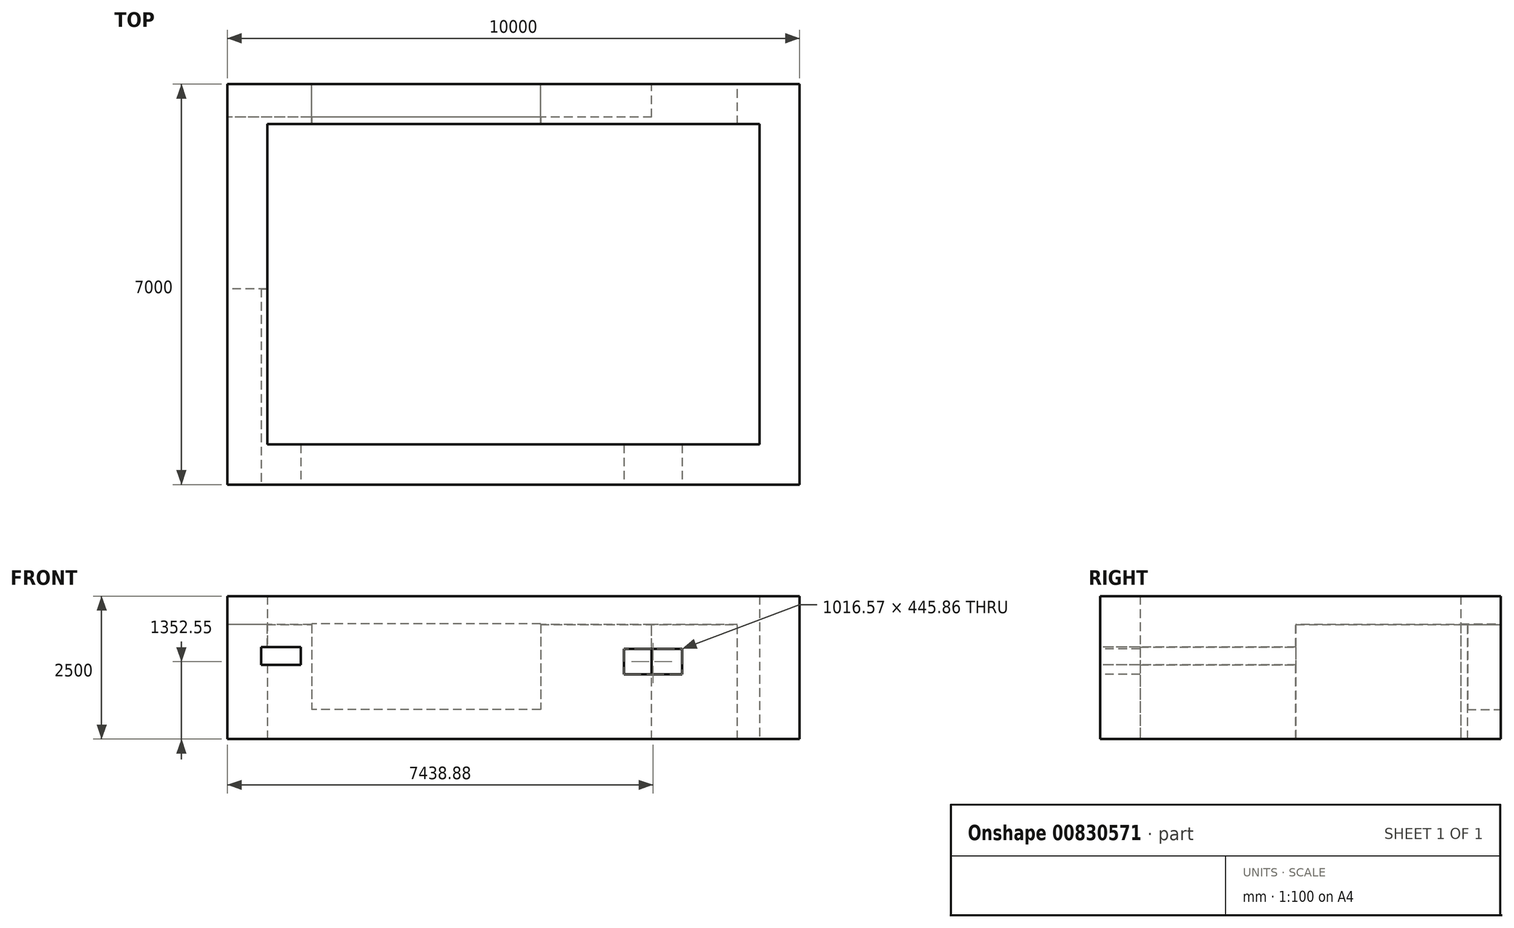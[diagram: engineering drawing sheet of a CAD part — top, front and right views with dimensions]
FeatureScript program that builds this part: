
annotation { "Feature Type Name" : "Feature", "Feature Type Description" : "" }
export const myFeature = defineFeature(function(context is Context, id is Id, definition is map)
    precondition{}
    {
        {
            var Q0;
            Q0=qCreatedBy(makeId("Top.planeOp"),FACE);
            var sketch = newSketch(context, id + "F0", { "sketchPlane" : qUnion([Q0])});
            skLineSegment(sketch, "E0.bottom", {"start": v(0, 0) * mm, "end": v(10000, 0) * mm});
            skLineSegment(sketch, "E0.top", {"start": v(0, 7000) * mm, "end": v(10000, 7000) * mm});
            skLineSegment(sketch, "E0.left", {"start": v(0, 0) * mm, "end": v(0, 7000) * mm});
            skLineSegment(sketch, "E0.right", {"start": v(10000, 0) * mm, "end": v(10000, 7000) * mm});
            skLineSegment(sketch, "E1.0", {"start": v(700, 700) * mm, "end": v(700, 6300) * mm});
            skLineSegment(sketch, "E1.1", {"start": v(700, 700) * mm, "end": v(9300, 700) * mm});
            skLineSegment(sketch, "E1.2", {"start": v(9300, 700) * mm, "end": v(9300, 6300) * mm});
            skLineSegment(sketch, "E1.3", {"start": v(700, 6300) * mm, "end": v(9300, 6300) * mm});
            skLineSegment(sketch, "E2.bottom", {"start": v(9294.84, 7000) * mm, "end": v(9300, 7000) * mm});
            skLineSegment(sketch, "E2.top", {"start": v(9294.84, 6300) * mm, "end": v(9300, 6300) * mm});
            skLineSegment(sketch, "E2.left", {"start": v(9294.84, 7000) * mm, "end": v(9294.84, 6300) * mm});
            skLineSegment(sketch, "E2.right", {"start": v(9300, 7000) * mm, "end": v(9300, 6300) * mm});
            skSolve(sketch);
        }
        {
            var Q0;
            Q0 = qSketchRegion(id + "F0", true);
            extrude(context, id + "F1", {"entities" : qUnion([Q0]), "depth" : 2500 * mm, "offsetDistance" : 25 * mm});
        }
        {
            var Q0;
            Q0=makeQuery(id+"F1.opExtrude","SWEPT_FACE",FACE,{"disambiguationData":[OSD([sQuery(id+"F0.wireOp",EDGE,"E0.top"),sQuery(id+"F0.wireOp",EDGE,"E2.bottom")])]});
            var sketch = newSketch(context, id + "F2", { "sketchPlane" : qUnion([Q0])});
            skLineSegment(sketch, "E3.bottom", {"start": v(-8914.27, 0) * mm, "end": v(-7414.27, 0) * mm});
            skLineSegment(sketch, "E3.top", {"start": v(-8914.27, 2000) * mm, "end": v(-7414.27, 2000) * mm});
            skLineSegment(sketch, "E3.left", {"start": v(-8914.27, 0) * mm, "end": v(-8914.27, 2000) * mm});
            skLineSegment(sketch, "E3.right", {"start": v(-7414.27, 0) * mm, "end": v(-7414.27, 2000) * mm});
            skLineSegment(sketch, "E4.bottom", {"start": v(-5473.14, 2015.1) * mm, "end": v(-1473.14, 2015.1) * mm});
            skLineSegment(sketch, "E4.top", {"start": v(-5473.14, 515.1) * mm, "end": v(-1473.14, 515.1) * mm});
            skLineSegment(sketch, "E4.left", {"start": v(-5473.14, 2015.1) * mm, "end": v(-5473.14, 515.1) * mm});
            skLineSegment(sketch, "E4.right", {"start": v(-1473.14, 2015.1) * mm, "end": v(-1473.14, 515.1) * mm});
            skSolve(sketch);
        }
        {
            var Q0;
            Q0=makeQuery(id+"F2.imprint","IMPRINT",FACE,{"disambiguationData":[TD([[makeQuery(id+"F2.imprint","IMPRINT",EDGE,{"derivedFrom":sQuery(id+"F2.wireOp",EDGE,"E3.bottom")}),-1.0]])]});
            var Q1;
            Q1=makeQuery(id+"F2.imprint","IMPRINT",FACE,{"disambiguationData":[TD([[makeQuery(id+"F2.imprint","IMPRINT",EDGE,{"derivedFrom":sQuery(id+"F2.wireOp",EDGE,"E4.bottom")}),-1.0]])]});
            extrude(context, id + "F3", {"entities" : qUnion([Q0, Q1]), "operationType" : NewBodyOperationType.REMOVE, "endBound" : BoundingType.UP_TO_NEXT, "oppositeDirection" : true, "depth" : 25 * mm, "offsetDistance" : 25 * mm});
        }
        {
            var Q0;
            Q0=makeQuery(id+"F1.opExtrude","SWEPT_FACE",FACE,{"disambiguationData":[OSD([sQuery(id+"F0.wireOp",EDGE,"E0.left")])]});
            var sketch = newSketch(context, id + "F4", { "sketchPlane" : qUnion([Q0])});
            skLineSegment(sketch, "E5.bottom", {"start": v(-6420.84, 2000) * mm, "end": v(-3420.84, 2000) * mm});
            skLineSegment(sketch, "E5.top", {"start": v(-6420.84, 0) * mm, "end": v(-3420.84, 0) * mm});
            skLineSegment(sketch, "E5.left", {"start": v(-6420.84, 2000) * mm, "end": v(-6420.84, 0) * mm});
            skLineSegment(sketch, "E5.right", {"start": v(-3420.84, 2000) * mm, "end": v(-3420.84, 0) * mm});
            skSolve(sketch);
        }
        {
            var Q0;
            Q0=makeQuery(id+"F4.imprint","IMPRINT",FACE,{"disambiguationData":[TD([[makeQuery(id+"F4.imprint","IMPRINT",EDGE,{"derivedFrom":sQuery(id+"F4.wireOp",EDGE,"E5.bottom")}),-1.0]])]});
            extrude(context, id + "F5", {"entities" : qUnion([Q0]), "operationType" : NewBodyOperationType.REMOVE, "endBound" : BoundingType.UP_TO_NEXT, "oppositeDirection" : true, "depth" : 25 * mm, "offsetDistance" : 25 * mm});
        }
        {
            var Q0;
            Q0=makeQuery(id+"F1.opExtrude","SWEPT_FACE",FACE,{"disambiguationData":[OSD([sQuery(id+"F0.wireOp",EDGE,"E0.bottom")])]});
            var sketch = newSketch(context, id + "F6", { "sketchPlane" : qUnion([Q0])});
            skLineSegment(sketch, "E6.bottom", {"start": v(590.4, 1611.15) * mm, "end": v(1285.95, 1611.15) * mm});
            skLineSegment(sketch, "E6.top", {"start": v(590.4, 1299.05) * mm, "end": v(1285.95, 1299.05) * mm});
            skLineSegment(sketch, "E6.left", {"start": v(590.4, 1611.15) * mm, "end": v(590.4, 1299.05) * mm});
            skLineSegment(sketch, "E6.right", {"start": v(1285.95, 1611.15) * mm, "end": v(1285.95, 1299.05) * mm});
            skLineSegment(sketch, "E7.bottom", {"start": v(6930.6, 1575.48) * mm, "end": v(7947.16, 1575.48) * mm});
            skLineSegment(sketch, "E7.top", {"start": v(6930.6, 1129.62) * mm, "end": v(7947.16, 1129.62) * mm});
            skLineSegment(sketch, "E7.left", {"start": v(6930.6, 1575.48) * mm, "end": v(6930.6, 1129.62) * mm});
            skLineSegment(sketch, "E7.right", {"start": v(7947.16, 1575.48) * mm, "end": v(7947.16, 1129.62) * mm});
            skSolve(sketch);
        }
        {
            var Q0;
            Q0=makeQuery(id+"F6.imprint","IMPRINT",FACE,{"disambiguationData":[TD([[makeQuery(id+"F6.imprint","IMPRINT",EDGE,{"derivedFrom":sQuery(id+"F6.wireOp",EDGE,"E6.bottom")}),-1.0]])]});
            var Q1;
            Q1=makeQuery(id+"F6.imprint","IMPRINT",FACE,{"disambiguationData":[TD([[makeQuery(id+"F6.imprint","IMPRINT",EDGE,{"derivedFrom":sQuery(id+"F6.wireOp",EDGE,"E7.bottom")}),-1.0]])]});
            extrude(context, id + "F7", {"entities" : qUnion([Q0, Q1]), "operationType" : NewBodyOperationType.REMOVE, "endBound" : BoundingType.UP_TO_NEXT, "oppositeDirection" : true, "depth" : 25 * mm, "offsetDistance" : 25 * mm});
        }
    });
